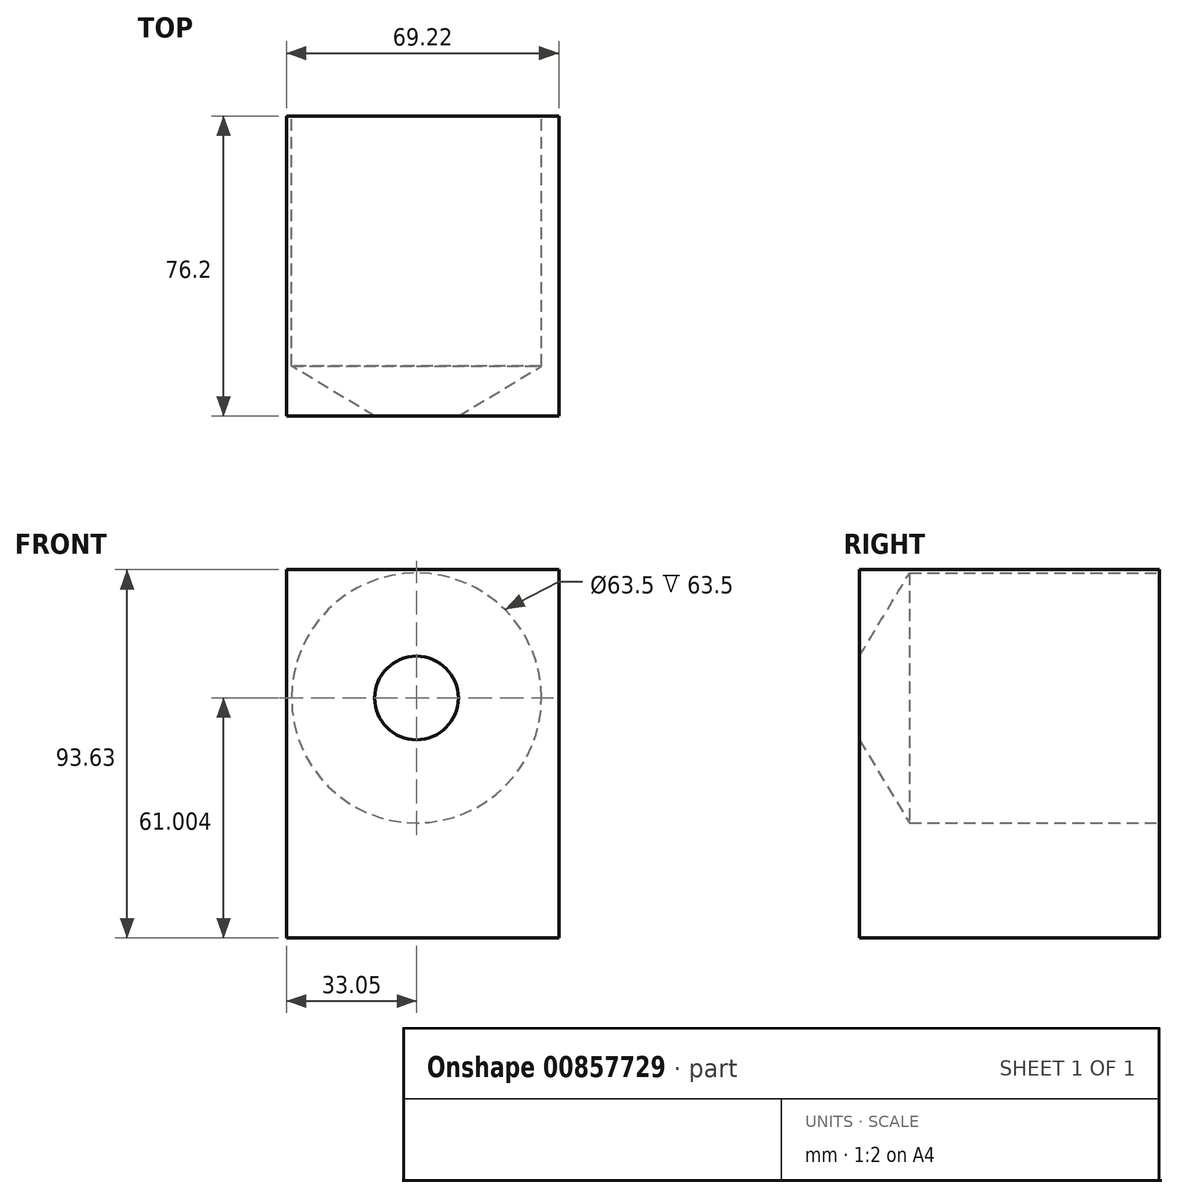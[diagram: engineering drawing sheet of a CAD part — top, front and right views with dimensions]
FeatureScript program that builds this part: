
annotation { "Feature Type Name" : "Feature", "Feature Type Description" : "" }
export const myFeature = defineFeature(function(context is Context, id is Id, definition is map)
    precondition{}
    {
        {
            var Q0;
            Q0=qCreatedBy(makeId("Front.planeOp"),FACE);
            var sketch = newSketch(context, id + "F0", { "sketchPlane" : qUnion([Q0])});
            skLineSegment(sketch, "E0.bottom", {"start": v(-33.05, 53.48) * mm, "end": v(36.17, 53.48) * mm});
            skLineSegment(sketch, "E0.top", {"start": v(-33.05, -40.15) * mm, "end": v(36.17, -40.15) * mm});
            skLineSegment(sketch, "E0.left", {"start": v(-33.05, 53.48) * mm, "end": v(-33.05, -40.15) * mm});
            skLineSegment(sketch, "E0.right", {"start": v(36.17, 53.48) * mm, "end": v(36.17, -40.15) * mm});
            skSolve(sketch);
        }
        {
            var Q0;
            Q0=qCreatedBy(makeId("Front.planeOp"),FACE);
            var sketch = newSketch(context, id + "F1", { "sketchPlane" : qUnion([Q0])});
            skCircle(sketch, "E1", {"center": v(0, 20.85) * mm, "radius": 26.97 * mm});
            skLineSegment(sketch, "E2.bottom", {"start": v(-24.54, -17.45) * mm, "end": v(-6.95, -17.45) * mm});
            skLineSegment(sketch, "E2.top", {"start": v(-24.54, -33.62) * mm, "end": v(-6.95, -33.62) * mm});
            skLineSegment(sketch, "E2.left", {"start": v(-24.54, -17.45) * mm, "end": v(-24.54, -33.62) * mm});
            skLineSegment(sketch, "E2.right", {"start": v(-6.95, -17.45) * mm, "end": v(-6.95, -33.62) * mm});
            skLineSegment(sketch, "E3.bottom", {"start": v(13.76, -17.45) * mm, "end": v(31.07, -17.45) * mm});
            skLineSegment(sketch, "E3.top", {"start": v(13.76, -34.19) * mm, "end": v(31.07, -34.19) * mm});
            skLineSegment(sketch, "E3.left", {"start": v(13.76, -17.45) * mm, "end": v(13.76, -34.19) * mm});
            skLineSegment(sketch, "E3.right", {"start": v(31.07, -17.45) * mm, "end": v(31.07, -34.19) * mm});
            skSolve(sketch);
        }
        {
            var Q0;
            Q0=qSketchRegion(id+"F0",true);
            extrude(context, id + "F2", {"entities" : qUnion([Q0]), "depth" : 76.2 * mm, "offsetDistance" : 25.4 * mm});
        }
        {
            var Q0;
            Q0=sQuery(id+"F1.wireOp",VERTEX,"E1.center");
            var Q1;
            Q1=makeQuery(id+"F2.opExtrude","SWEPT_BODY",BODY,{"disambiguationData":[OSD([sQuery(id+"F0.wireOp",EDGE,"E0.bottom"),sQuery(id+"F0.wireOp",EDGE,"E0.top"),sQuery(id+"F0.wireOp",EDGE,"E0.left"),sQuery(id+"F0.wireOp",EDGE,"E0.right")])]});
            hole(context, id + "F3", {"style" : HoleStyle.SIMPLE, "endStyle" : HoleEndStyle.BLIND, "oppositeDirection" : true, "holeDiameter" : 63.5 * mm, "majorDiameter" : 6.35 * mm, "holeDepth" : 63.5 * mm, "isTappedThrough" : true, "tappedDepth" : 12.7 * mm, "tapClearance" : 3, "locations" : qUnion([Q0]), "scope" : qUnion([Q1])});
        }
    });
